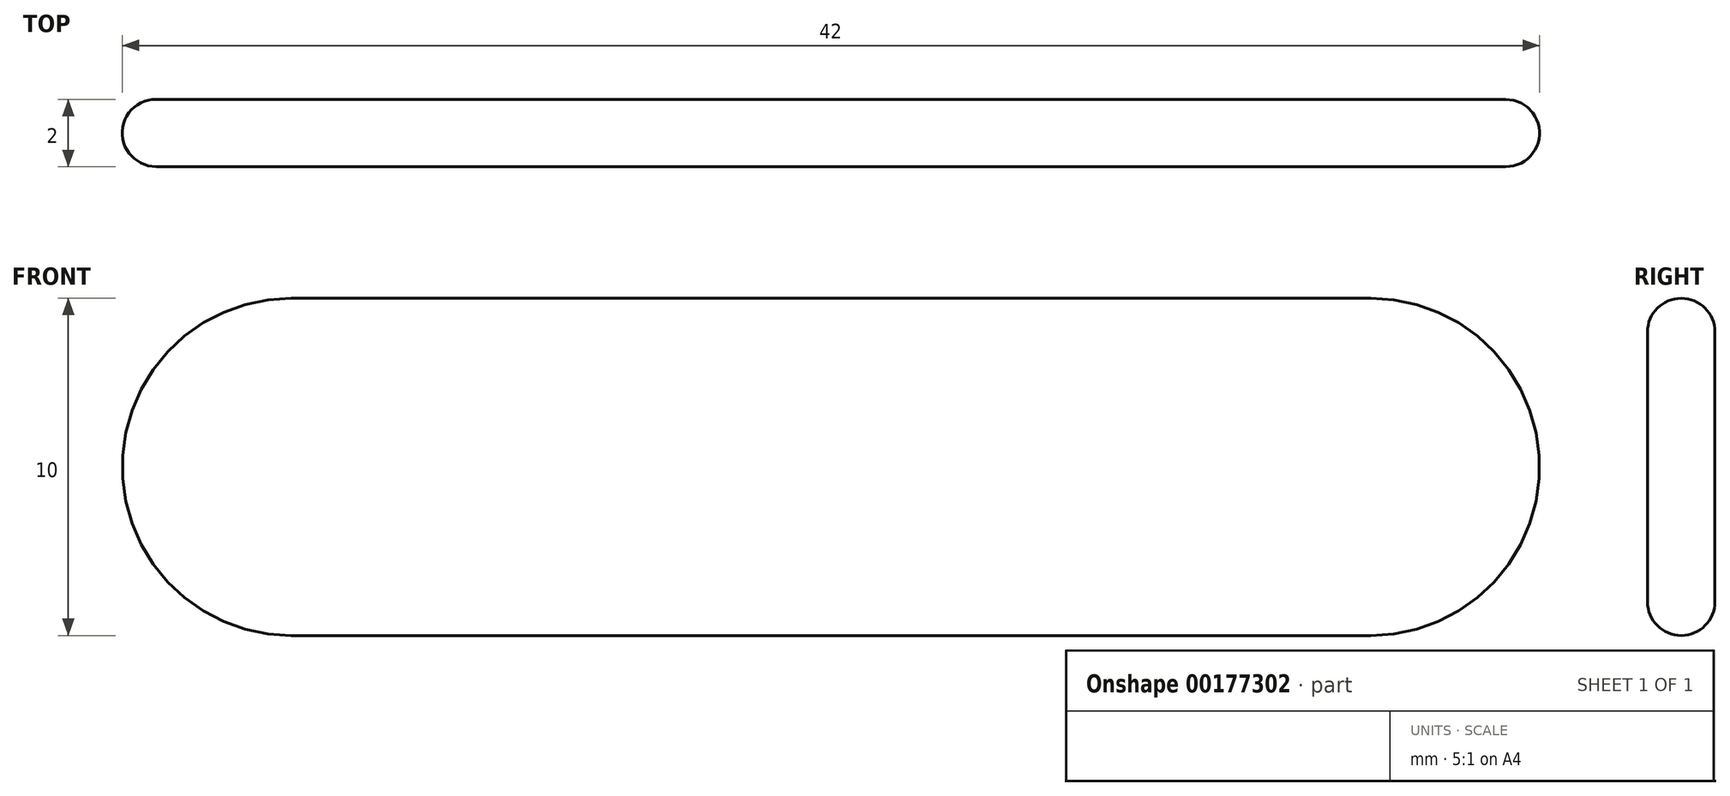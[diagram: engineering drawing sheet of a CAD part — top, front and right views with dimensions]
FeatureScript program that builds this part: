
annotation { "Feature Type Name" : "Feature", "Feature Type Description" : "" }
export const myFeature = defineFeature(function(context is Context, id is Id, definition is map)
    precondition{}
    {
        {
            var Q0;
            Q0=qCreatedBy(makeId("Front.planeOp"),FACE);
            var sketch = newSketch(context, id + "F0", { "sketchPlane" : qUnion([Q0])});
            skLineSegment(sketch, "E0.bottom", {"start": v(-16, 5) * mm, "end": v(16, 5) * mm});
            skLineSegment(sketch, "E0.top", {"start": v(-16, -5) * mm, "end": v(16, -5) * mm});
            skLineSegment(sketch, "E0.left", {"start": v(-21, 0) * mm, "end": v(-21, 0) * mm});
            skLineSegment(sketch, "E0.right", {"start": v(21, 0) * mm, "end": v(21, 0) * mm});
            skPoint(sketch, "E0.middle", {"position": v(0, 0) * mm});
            skPoint(sketch, "E1.visualSharp", {"position": v(-21, 5) * mm});
            skArc(sketch, "E1.filletArc", {"start": v(-16, 5) * mm, "mid": v(-19.54, 3.54) * mm, "end": v(-21, 0) * mm});
            skPoint(sketch, "E2.visualSharp", {"position": v(-21, -5) * mm});
            skArc(sketch, "E2.filletArc", {"start": v(-21, 0) * mm, "mid": v(-19.54, -3.54) * mm, "end": v(-16, -5) * mm});
            skPoint(sketch, "E3.visualSharp", {"position": v(21, 5) * mm});
            skArc(sketch, "E3.filletArc", {"start": v(21, 0) * mm, "mid": v(19.54, 3.54) * mm, "end": v(16, 5) * mm});
            skPoint(sketch, "E4.visualSharp", {"position": v(21, -5) * mm});
            skArc(sketch, "E4.filletArc", {"start": v(16, -5) * mm, "mid": v(19.54, -3.54) * mm, "end": v(21, 0) * mm});
            skSolve(sketch);
        }
        {
            var Q0;
            Q0 = qSketchRegion(id + "F0", true);
            extrude(context, id + "F1", {"entities" : qUnion([Q0]), "depth" : 2 * mm});
        }
        {
            var Q0;
            Q0=makeQuery(id+"F1.opExtrude","CAP_FACE",FACE,{"disambiguationData":[OSD([sQuery(id+"F0.wireOp",EDGE,"E0.bottom"),sQuery(id+"F0.wireOp",EDGE,"E0.top"),sQuery(id+"F0.wireOp",EDGE,"E1.filletArc"),sQuery(id+"F0.wireOp",EDGE,"E2.filletArc"),sQuery(id+"F0.wireOp",EDGE,"E3.filletArc"),sQuery(id+"F0.wireOp",EDGE,"E4.filletArc")])],"isStart":false});
            var Q1;
            Q1=makeQuery(id+"F1.opExtrude","CAP_FACE",FACE,{"disambiguationData":[OSD([sQuery(id+"F0.wireOp",EDGE,"E0.bottom"),sQuery(id+"F0.wireOp",EDGE,"E0.top"),sQuery(id+"F0.wireOp",EDGE,"E1.filletArc"),sQuery(id+"F0.wireOp",EDGE,"E2.filletArc"),sQuery(id+"F0.wireOp",EDGE,"E3.filletArc"),sQuery(id+"F0.wireOp",EDGE,"E4.filletArc")])],"isStart":true});
            fillet(context, id + "F2", {"entities" : qUnion([Q0, Q1]), "radius" : 1 * mm, "tangentPropagation" : true, "allowEdgeOverflow" : false});
        }
    });
